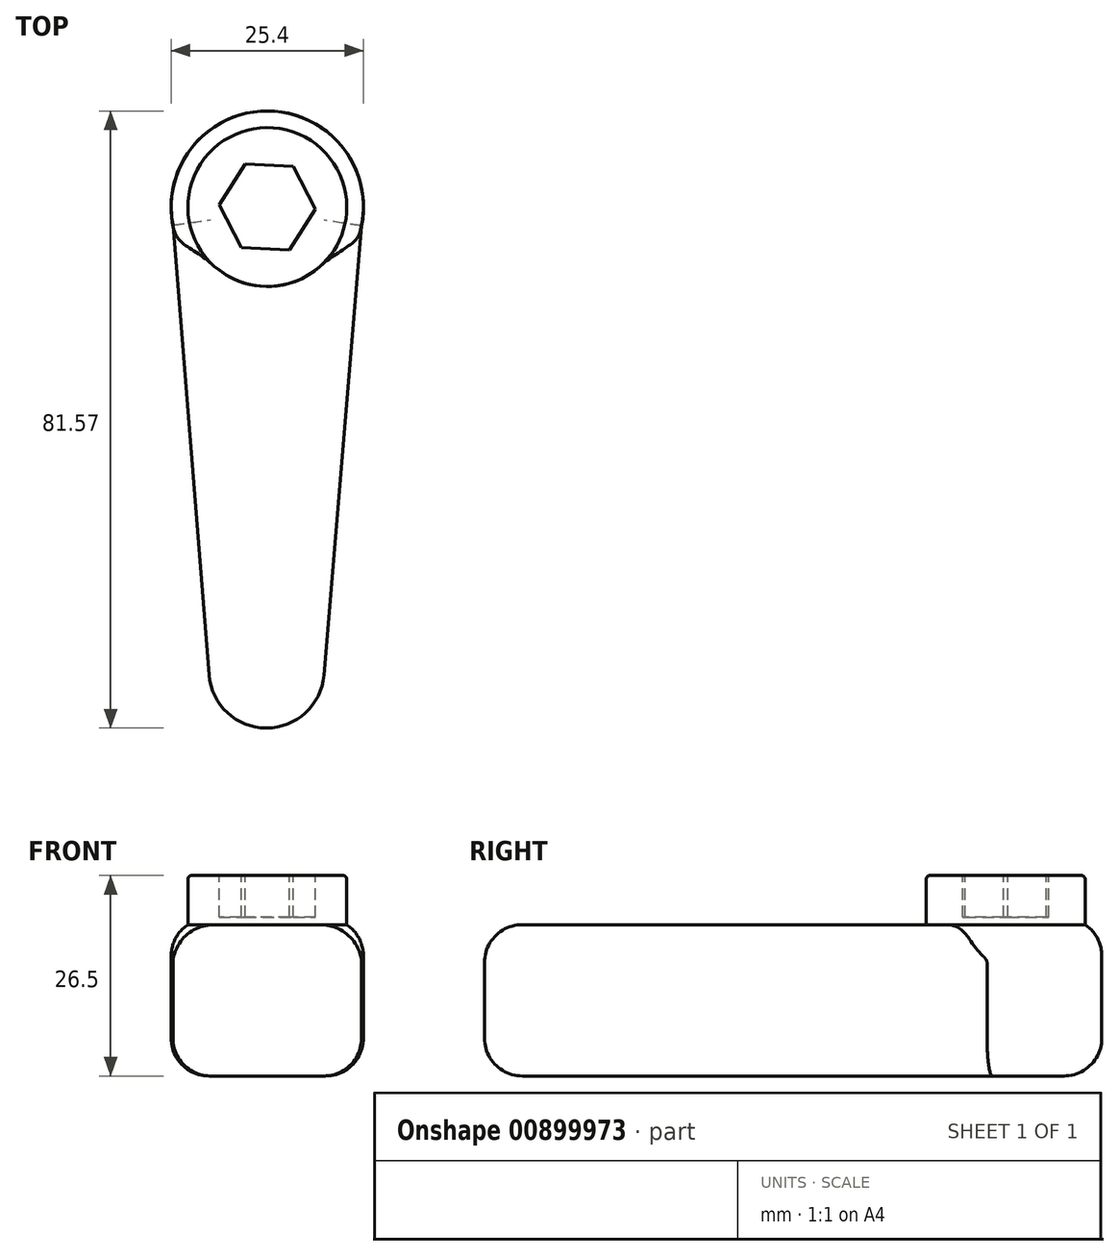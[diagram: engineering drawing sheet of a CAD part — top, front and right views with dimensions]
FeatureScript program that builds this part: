
annotation { "Feature Type Name" : "Feature", "Feature Type Description" : "" }
export const myFeature = defineFeature(function(context is Context, id is Id, definition is map)
    precondition{}
    {
        {
            var Q0;
            Q0=qCreatedBy(makeId("Top.planeOp"),FACE);
            var sketch = newSketch(context, id + "F0", { "sketchPlane" : qUnion([Q0])});
            skCircle(sketch, "E0", {"center": v(0.11, 55) * mm, "radius": 12.7 * mm});
            skCircle(sketch, "E1", {"center": v(0, -6.25) * mm, "radius": 7.62 * mm});
            skLineSegment(sketch, "E2", {"start": v(-12.58, 55.37) * mm, "end": v(-7.6, -6.86) * mm});
            skLineSegment(sketch, "E3", {"start": v(12.8, 55.37) * mm, "end": v(7.6, -6.89) * mm});
            skSolve(sketch);
        }
        {
            var Q0;
            Q0 = qSketchRegion(id + "F0", true);
            extrude(context, id + "F1", {"entities" : qUnion([Q0]), "depth" : 20 * mm, "offsetDistance" : 25 * mm});
        }
        {
            var Q0;
            Q0=makeQuery(id+"F1.opExtrude","CAP_FACE",FACE,{"disambiguationData":[OSD([sQuery(id+"F0.wireOp",EDGE,"E0"),sQuery(id+"F0.wireOp",EDGE,"E1"),sQuery(id+"F0.wireOp",EDGE,"E2"),sQuery(id+"F0.wireOp",EDGE,"E3")])],"isStart":false});
            var sketch = newSketch(context, id + "F2", { "sketchPlane" : qUnion([Q0])});
            skCircle(sketch, "E4", {"center": v(0.11, 55) * mm, "radius": 10.5 * mm});
            skSolve(sketch);
        }
        {
            var Q0;
            Q0 = qSketchRegion(id + "F2", true);
            extrude(context, id + "F3", {"entities" : qUnion([Q0]), "operationType" : NewBodyOperationType.ADD, "depth" : 6.5 * mm, "offsetDistance" : 25 * mm});
        }
        {
            var Q0;
            Q0=makeQuery(id+"F3.opExtrude","CAP_FACE",FACE,{"disambiguationData":[OSD([sQuery(id+"F2.wireOp",EDGE,"E4")])],"isStart":false});
            var sketch = newSketch(context, id + "F4", { "sketchPlane" : qUnion([Q0])});
            skCircle(sketch, "E5.cCircle", {"center": v(0.11, 55) * mm, "radius": 5.53 * mm, "construction": true});
            skLineSegment(sketch, "E5.0", {"start": v(6.48, 54.71) * mm, "end": v(3.05, 49.34) * mm});
            skLineSegment(sketch, "E5.1", {"start": v(3.05, 49.34) * mm, "end": v(-3.32, 49.62) * mm});
            skLineSegment(sketch, "E5.2", {"start": v(-3.32, 49.62) * mm, "end": v(-6.26, 55.29) * mm});
            skLineSegment(sketch, "E5.3", {"start": v(-6.26, 55.29) * mm, "end": v(-2.83, 60.66) * mm});
            skLineSegment(sketch, "E5.4", {"start": v(-2.83, 60.66) * mm, "end": v(3.55, 60.38) * mm});
            skLineSegment(sketch, "E5.5", {"start": v(3.55, 60.38) * mm, "end": v(6.48, 54.71) * mm});
            skPoint(sketch, "E5.0.midPoint", {"position": v(4.77, 52.03) * mm});
            skSolve(sketch);
        }
        {
            var Q0;
            Q0 = qSketchRegion(id + "F4", true);
            extrude(context, id + "F5", {"entities" : qUnion([Q0]), "operationType" : NewBodyOperationType.REMOVE, "oppositeDirection" : true, "depth" : 5.5 * mm, "offsetDistance" : 25 * mm});
        }
        {
            var Q0;
            Q0=makeQuery(id+"F1.opExtrude","CAP_EDGE",EDGE,{"disambiguationData":[OSD([sQuery(id+"F0.wireOp",EDGE,"E3")])],"isStart":false});
            var Q1;
            Q1=makeQuery(id+"F1.opExtrude","CAP_EDGE",EDGE,{"disambiguationData":[OSD([sQuery(id+"F0.wireOp",EDGE,"E2")])],"isStart":true});
            var Q2;
            Q2=makeQuery(id+"F1.opExtrude","CAP_EDGE",EDGE,{"disambiguationData":[OSD([sQuery(id+"F0.wireOp",EDGE,"E0")])],"isStart":true});
            fillet(context, id + "F6", {"entities" : qUnion([Q0, Q1, Q2]), "radius" : 5 * mm, "tangentPropagation" : true, "allowEdgeOverflow" : false});
        }
        {
            var Q0;
            Q0=makeQuery(id+"F1.opExtrude","CAP_EDGE",EDGE,{"disambiguationData":[OSD([sQuery(id+"F0.wireOp",EDGE,"E0")])],"isStart":false});
            fillet(context, id + "F7", {"entities" : qUnion([Q0]), "radius" : 5 * mm, "tangentPropagation" : true, "allowEdgeOverflow" : false});
        }
        {
            var Q0;
            Q0=makeQuery(id+"F3.opExtrude","CAP_EDGE",EDGE,{"disambiguationData":[OSD([sQuery(id+"F2.wireOp",EDGE,"E4")])],"isStart":false});
            fillet(context, id + "F8", {"entities" : qUnion([Q0]), "radius" : .5 * mm, "tangentPropagation" : true, "allowEdgeOverflow" : false});
        }
    });
